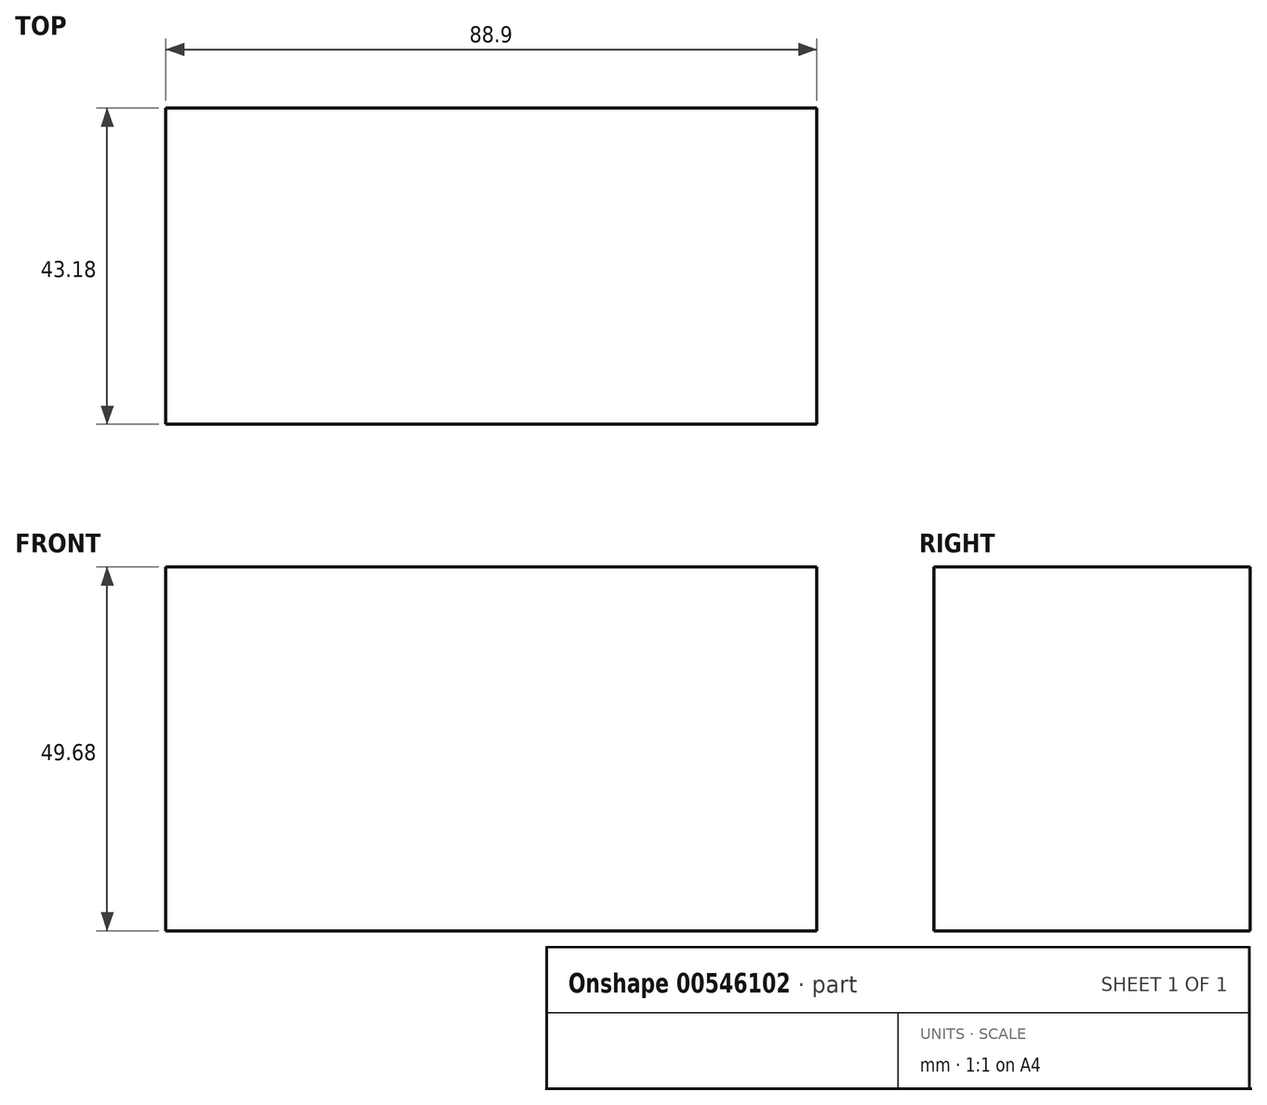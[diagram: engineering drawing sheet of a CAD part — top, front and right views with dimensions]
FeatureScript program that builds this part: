
annotation { "Feature Type Name" : "Feature", "Feature Type Description" : "" }
export const myFeature = defineFeature(function(context is Context, id is Id, definition is map)
    precondition{}
    {
        {
            var Q0;
            Q0=qCreatedBy(makeId("Front.planeOp"),FACE);
            var sketch = newSketch(context, id + "F0", { "sketchPlane" : qUnion([Q0])});
            skLineSegment(sketch, "E0.bottom", {"start": v(-44.45, 24.84) * mm, "end": v(44.45, 24.84) * mm});
            skLineSegment(sketch, "E0.top", {"start": v(-44.45, -24.84) * mm, "end": v(44.45, -24.84) * mm});
            skLineSegment(sketch, "E0.left", {"start": v(-44.45, 24.84) * mm, "end": v(-44.45, -24.84) * mm});
            skLineSegment(sketch, "E0.right", {"start": v(44.45, 24.84) * mm, "end": v(44.45, -24.84) * mm});
            skPoint(sketch, "E0.middle", {"position": v(0, 0) * mm});
            skSolve(sketch);
        }
        {
            var Q0;
            Q0=makeQuery(id+"F0.imprint","IMPRINT",FACE,{"disambiguationData":[TD([[makeQuery(id+"F0.imprint","IMPRINT",EDGE,{"derivedFrom":sQuery(id+"F0.wireOp",EDGE,"E0.bottom")}),-1.0]])]});
            extrude(context, id + "F1", {"entities" : qUnion([Q0]), "endBound" : BoundingType.SYMMETRIC, "depth" : 43.18 * mm, "offsetDistance" : 25.4 * mm});
        }
    });
